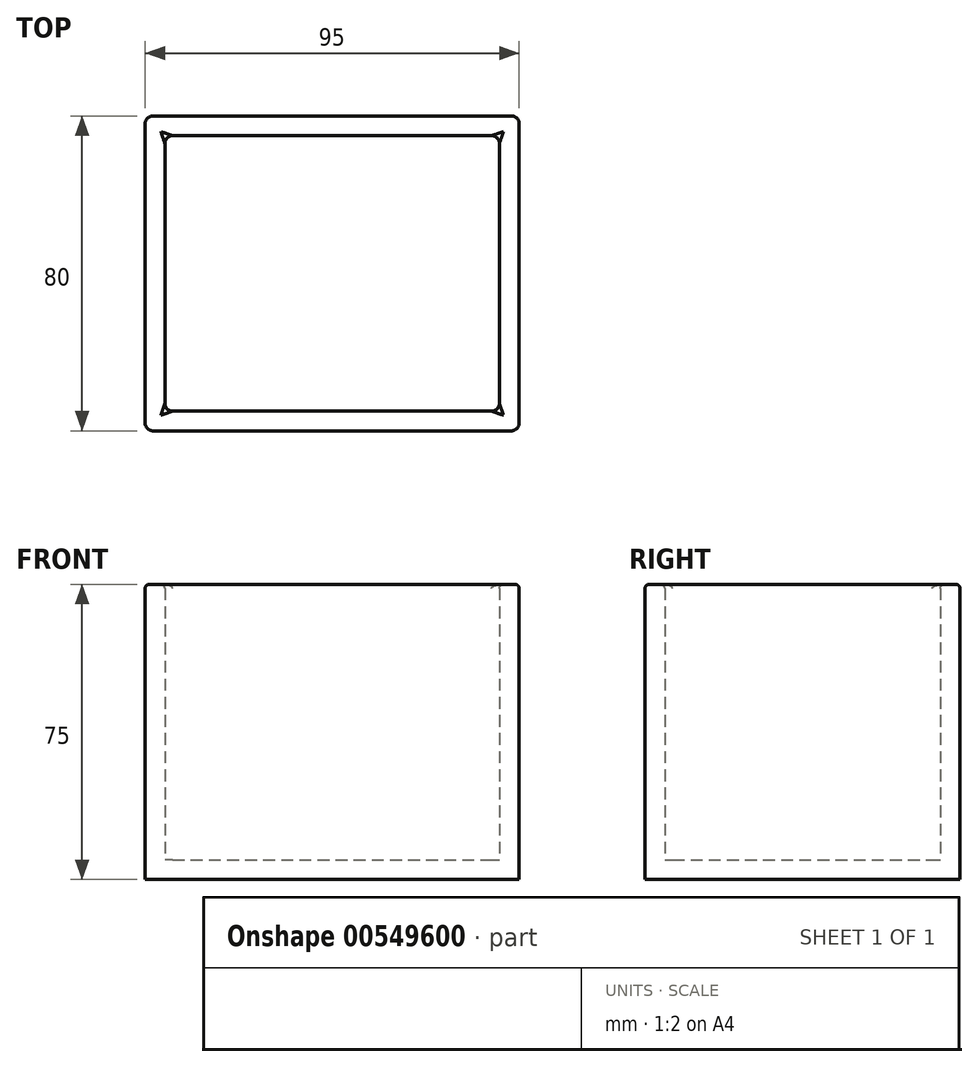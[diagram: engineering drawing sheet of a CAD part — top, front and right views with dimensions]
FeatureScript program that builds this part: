
annotation { "Feature Type Name" : "Feature", "Feature Type Description" : "" }
export const myFeature = defineFeature(function(context is Context, id is Id, definition is map)
    precondition{}
    {
        {
            var Q0;
            Q0=qCreatedBy(makeId("Front.planeOp"),FACE);
            var sketch = newSketch(context, id + "F0", { "sketchPlane" : qUnion([Q0])});
            skLineSegment(sketch, "E0.bottom", {"start": v(-45.07, 45.33) * mm, "end": v(49.93, 45.33) * mm});
            skLineSegment(sketch, "E0.top", {"start": v(-45.07, -29.67) * mm, "end": v(49.93, -29.67) * mm});
            skLineSegment(sketch, "E0.left", {"start": v(-45.07, 45.33) * mm, "end": v(-45.07, -29.67) * mm});
            skLineSegment(sketch, "E0.right", {"start": v(49.93, 45.33) * mm, "end": v(49.93, -29.67) * mm});
            skSolve(sketch);
        }
        {
            var Q0;
            Q0=makeQuery(id+"F0.imprint","IMPRINT",FACE,{"disambiguationData":[TD([[makeQuery(id+"F0.imprint","IMPRINT",EDGE,{"derivedFrom":sQuery(id+"F0.wireOp",EDGE,"E0.bottom")}),-1.0]])]});
            extrude(context, id + "F1", {"entities" : qUnion([Q0]), "depth" : 80 * mm, "offsetDistance" : 25 * mm});
        }
        {
            var Q0;
            Q0=makeQuery(id+"F1.opExtrude","SWEPT_FACE",FACE,{"disambiguationData":[OSD([sQuery(id+"F0.wireOp",EDGE,"E0.bottom")])]});
            shell(context, id + "F2", {"entities" : qUnion([Q0]), "thickness" : 5 * mm});
        }
        {
            var Q0;
            Q0=makeQuery(id+"F1.opExtrude","SWEPT_EDGE",EDGE,{"disambiguationData":[OSD([sQuery(id+"F0.wireOp",EDGE,"E0.bottom"),sQuery(id+"F0.wireOp",EDGE,"E0.left")])]});
            var Q1;
            Q1=makeQuery(id+"F2.opShell","OFFSET_EDGE",EDGE,{"disambiguationData":[OSD([sQuery(id+"F0.wireOp",EDGE,"E0.bottom"),sQuery(id+"F0.wireOp",EDGE,"E0.left")])]});
            var Q2;
            {var subQ0=sQuery(id+"F0.wireOp",EDGE,"E0.bottom");Q2=makeQuery(id+"F2.opShell","OFFSET_EDGE",EDGE,{"disambiguationData":[OSD([subQ0]),TDD([makeQuery(id+"F1.opExtrude","CAP_EDGE",EDGE,{"disambiguationData":[OSD([subQ0])],"isStart":true})])]});}
            var Q3;
            Q3=makeQuery(id+"F1.opExtrude","CAP_EDGE",EDGE,{"disambiguationData":[OSD([sQuery(id+"F0.wireOp",EDGE,"E0.bottom")])],"isStart":true});
            var Q4;
            Q4=makeQuery(id+"F2.opShell","OFFSET_EDGE",EDGE,{"disambiguationData":[OSD([sQuery(id+"F0.wireOp",EDGE,"E0.bottom"),sQuery(id+"F0.wireOp",EDGE,"E0.right")])]});
            var Q5;
            Q5=makeQuery(id+"F1.opExtrude","SWEPT_EDGE",EDGE,{"disambiguationData":[OSD([sQuery(id+"F0.wireOp",EDGE,"E0.bottom"),sQuery(id+"F0.wireOp",EDGE,"E0.right")])]});
            var Q6;
            {var subQ0=sQuery(id+"F0.wireOp",EDGE,"E0.bottom");Q6=makeQuery(id+"F2.opShell","OFFSET_EDGE",EDGE,{"disambiguationData":[OSD([subQ0]),TDD([makeQuery(id+"F1.opExtrude","CAP_EDGE",EDGE,{"disambiguationData":[OSD([subQ0])],"isStart":false})])]});}
            var Q7;
            Q7=makeQuery(id+"F1.opExtrude","CAP_EDGE",EDGE,{"disambiguationData":[OSD([sQuery(id+"F0.wireOp",EDGE,"E0.bottom")])],"isStart":false});
            fillet(context, id + "F3", {"entities" : qUnion([Q0, Q1, Q2, Q3, Q4, Q5, Q6, Q7]), "radius" : 1 * mm, "tangentPropagation" : true, "allowEdgeOverflow" : false});
        }
        {
            var Q0;
            Q0=makeQuery(id+"F1.opExtrude","CAP_EDGE",EDGE,{"disambiguationData":[OSD([sQuery(id+"F0.wireOp",EDGE,"E0.left")])],"isStart":false});
            var Q1;
            Q1=makeQuery(id+"F1.opExtrude","CAP_EDGE",EDGE,{"disambiguationData":[OSD([sQuery(id+"F0.wireOp",EDGE,"E0.right")])],"isStart":false});
            var Q2;
            Q2=makeQuery(id+"F1.opExtrude","CAP_EDGE",EDGE,{"disambiguationData":[OSD([sQuery(id+"F0.wireOp",EDGE,"E0.right")])],"isStart":true});
            var Q3;
            Q3=makeQuery(id+"F1.opExtrude","CAP_EDGE",EDGE,{"disambiguationData":[OSD([sQuery(id+"F0.wireOp",EDGE,"E0.left")])],"isStart":true});
            fillet(context, id + "F4", {"entities" : qUnion([Q0, Q1, Q2, Q3]), "radius" : 2 * mm, "tangentPropagation" : true, "allowEdgeOverflow" : false});
        }
        {
            var Q0;
            {var subQ0=sQuery(id+"F0.wireOp",EDGE,"E0.left");Q0=makeQuery(id+"F2.opShell","OFFSET_EDGE",EDGE,{"disambiguationData":[OSD([subQ0]),TDD([makeQuery(id+"F1.opExtrude","CAP_EDGE",EDGE,{"disambiguationData":[OSD([subQ0])],"isStart":true})])]});}
            var Q1;
            {var subQ0=sQuery(id+"F0.wireOp",EDGE,"E0.right");Q1=makeQuery(id+"F2.opShell","OFFSET_EDGE",EDGE,{"disambiguationData":[OSD([subQ0]),TDD([makeQuery(id+"F1.opExtrude","CAP_EDGE",EDGE,{"disambiguationData":[OSD([subQ0])],"isStart":true})])]});}
            var Q2;
            {var subQ0=sQuery(id+"F0.wireOp",EDGE,"E0.left");Q2=makeQuery(id+"F2.opShell","OFFSET_EDGE",EDGE,{"disambiguationData":[OSD([subQ0]),TDD([makeQuery(id+"F1.opExtrude","CAP_EDGE",EDGE,{"disambiguationData":[OSD([subQ0])],"isStart":false})])]});}
            var Q3;
            {var subQ0=sQuery(id+"F0.wireOp",EDGE,"E0.right");Q3=makeQuery(id+"F2.opShell","OFFSET_EDGE",EDGE,{"disambiguationData":[OSD([subQ0]),TDD([makeQuery(id+"F1.opExtrude","CAP_EDGE",EDGE,{"disambiguationData":[OSD([subQ0])],"isStart":false})])]});}
            fillet(context, id + "F5", {"entities" : qUnion([Q0, Q1, Q2, Q3]), "radius" : 2 * mm, "tangentPropagation" : true, "allowEdgeOverflow" : false});
        }
    });
